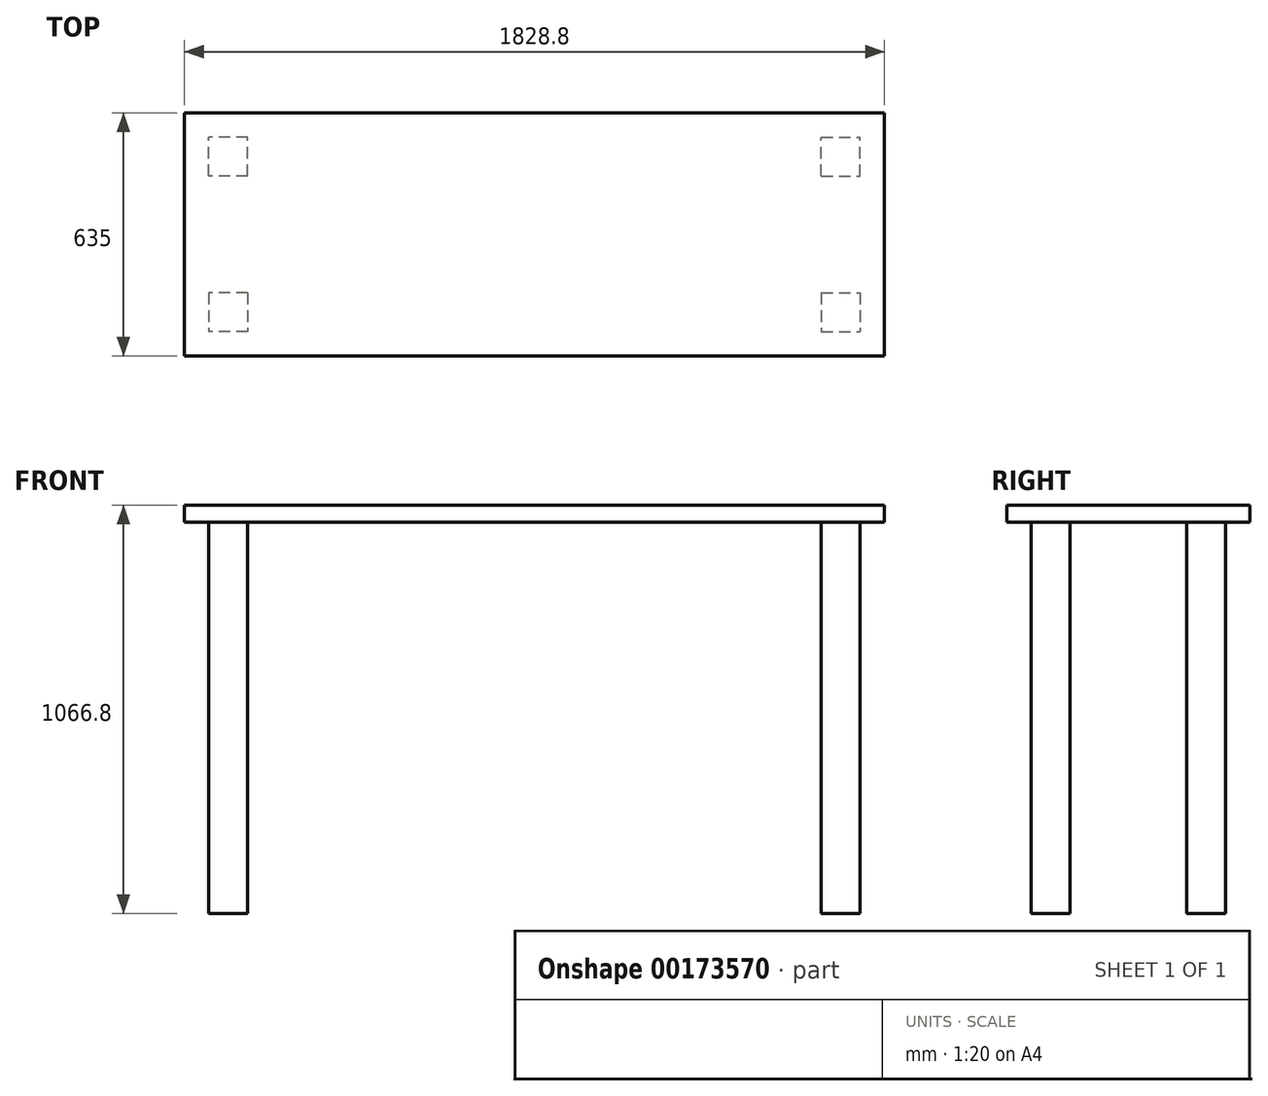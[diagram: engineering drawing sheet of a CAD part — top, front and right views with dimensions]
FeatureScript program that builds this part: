
annotation { "Feature Type Name" : "Feature", "Feature Type Description" : "" }
export const myFeature = defineFeature(function(context is Context, id is Id, definition is map)
    precondition{}
    {
        {
            var Q0;
            Q0=qCreatedBy(makeId("Top.planeOp"),FACE);
            var sketch = newSketch(context, id + "F0", { "sketchPlane" : qUnion([Q0])});
            skLineSegment(sketch, "E0.bottom", {"start": v(914.4, -317.5) * mm, "end": v(-914.4, -317.5) * mm});
            skLineSegment(sketch, "E0.top", {"start": v(914.4, 317.5) * mm, "end": v(-914.4, 317.5) * mm});
            skLineSegment(sketch, "E0.left", {"start": v(914.4, -317.5) * mm, "end": v(914.4, 317.5) * mm});
            skLineSegment(sketch, "E0.right", {"start": v(-914.4, -317.5) * mm, "end": v(-914.4, 317.5) * mm});
            skPoint(sketch, "E0.middle", {"position": v(0, 0) * mm});
            skSolve(sketch);
        }
        {
            var Q0;
            Q0=makeQuery(id+"F0.imprint","IMPRINT",FACE,{"disambiguationData":[TD([[makeQuery(id+"F0.imprint","IMPRINT",EDGE,{"derivedFrom":sQuery(id+"F0.wireOp",EDGE,"E0.bottom")}),-1.0]])]});
            extrude(context, id + "F1", {"entities" : qUnion([Q0]), "depth" : 44.45 * mm});
        }
        {
            var Q0;
            Q0=makeQuery(id+"F1.opExtrude","CAP_FACE",FACE,{"disambiguationData":[OSD([sQuery(id+"F0.wireOp",EDGE,"E0.bottom"),sQuery(id+"F0.wireOp",EDGE,"E0.top"),sQuery(id+"F0.wireOp",EDGE,"E0.left"),sQuery(id+"F0.wireOp",EDGE,"E0.right")])],"isStart":true});
            var sketch = newSketch(context, id + "F2", { "sketchPlane" : qUnion([Q0])});
            skLineSegment(sketch, "E1.bottom", {"start": v(-749.3, -152.4) * mm, "end": v(-850.9, -152.4) * mm});
            skLineSegment(sketch, "E1.top", {"start": v(-749.3, -254) * mm, "end": v(-850.9, -254) * mm});
            skLineSegment(sketch, "E1.left", {"start": v(-749.3, -152.4) * mm, "end": v(-749.3, -254) * mm});
            skLineSegment(sketch, "E1.right", {"start": v(-850.9, -152.4) * mm, "end": v(-850.9, -254) * mm});
            skPoint(sketch, "E1.middle", {"position": v(-800.1, -203.2) * mm});
            skLineSegment(sketch, "E2.MirrorCS", {"start": v(-749.3, 152.4) * mm, "end": v(-850.9, 152.4) * mm});
            skLineSegment(sketch, "E3.MirrorCS", {"start": v(-749.3, 152.4) * mm, "end": v(-749.3, 254) * mm});
            skLineSegment(sketch, "E4.MirrorCS", {"start": v(-850.9, 152.4) * mm, "end": v(-850.9, 254) * mm});
            skLineSegment(sketch, "E5.MirrorCS", {"start": v(-749.3, 254) * mm, "end": v(-850.9, 254) * mm});
            skLineSegment(sketch, "E6.MirrorCS", {"start": v(850.9, 152.4) * mm, "end": v(850.9, 254) * mm});
            skLineSegment(sketch, "E7.MirrorCS", {"start": v(749.3, 152.4) * mm, "end": v(749.3, 254) * mm});
            skLineSegment(sketch, "E8.MirrorCS", {"start": v(749.3, 254) * mm, "end": v(850.9, 254) * mm});
            skLineSegment(sketch, "E9.MirrorCS", {"start": v(749.3, 152.4) * mm, "end": v(850.9, 152.4) * mm});
            skPoint(sketch, "E10.MirrorP", {"position": v(800.1, -203.2) * mm});
            skLineSegment(sketch, "E11.MirrorCS", {"start": v(749.3, -152.4) * mm, "end": v(850.9, -152.4) * mm});
            skLineSegment(sketch, "E12.MirrorCS", {"start": v(749.3, -254) * mm, "end": v(850.9, -254) * mm});
            skLineSegment(sketch, "E13.MirrorCS", {"start": v(749.3, -152.4) * mm, "end": v(749.3, -254) * mm});
            skLineSegment(sketch, "E14.MirrorCS", {"start": v(850.9, -152.4) * mm, "end": v(850.9, -254) * mm});
            skSolve(sketch);
        }
        {
            var Q0;
            Q0 = qSketchRegion(id + "F2", true);
            extrude(context, id + "F3", {"entities" : qUnion([Q0]), "operationType" : NewBodyOperationType.ADD, "depth" : 1022.35 * mm});
        }
    });
